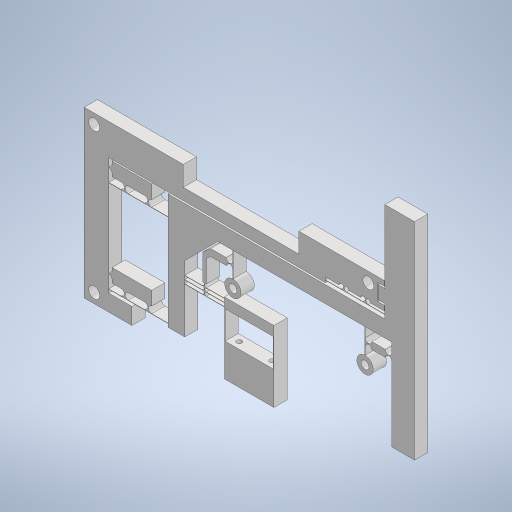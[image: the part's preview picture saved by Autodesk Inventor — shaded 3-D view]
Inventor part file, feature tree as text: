
AUTODESK INVENTOR PART (.ipt)
format: ipt  version: 2023 (Build 270158000, 158)  size: 674,816 bytes
history: native  units: mm
features: reference x11, extrude x9, sketch x8, other x7
ambient origin geometry x8: Origin, YZ Plane, XZ Plane, XY Plane, X Axis, Y Axis, Z Axis, Center Point
bodies: Solid1 (feature_tree)
feature tree (35):
  other  "<userpath>\ClawdDrive\Objet3D\IminaProbe\V3Roue\Settings.xlsx"
  extrude  "Extrusion1"  Depth=20.0mm
  extrude  "Extrusion2"  Depth=4.0mm TaperAngle=0.0deg
  extrude  "Extrusion3"  Depth=0.5mm
  extrude  "Extrusion4"  Depth=5.0mm
  extrude  "Extrusion5"  Depth=18.0mm
  extrude  "Extrusion7"  Depth=1.0mm
  extrude  "Extrusion8"  Depth=1.0mm
  extrude  "Extrusion9"  Depth=0.1mm
  extrude  "Extrusion10"  Depth=5.0mm
  sketch  "Sketch1"  dims[d0=4.0mm d1=0.0mm d2=20.0mm]
  reference  "Reference1"
  sketch  "Sketch2"  dims[d3=9.0mm d4=4.0mm d5=0.0mm]
  sketch  "Sketch6"  dims[d6=7.0mm d7=0.5mm]
  reference  "Reference2"
  sketch  "Sketch7"  dims[d8=4.0mm d9=0.0mm d27=5.0mm]
  sketch  "Sketch9"  dims[d28=30.0mm d29=18.0mm]
  sketch  "Sketch10"  dims[d30=0.1mm d31=1.0mm]
  sketch  "Sketch11"  dims[d32=0.1mm d33=1.0mm]
  reference  "Reference3"
  reference  "Reference4"
  reference  "Reference5"
  reference  "Reference6"
  reference  "Reference7"
  reference  "Reference8"
  sketch  "Sketch12"  dims[d34=15.0mm d35=0.1mm d37=5.0mm d39=5.0mm d40=0.1mm d41=0.1mm d43=0.0mm d44=15.0mm d45=18.0mm d46=2.0mm d47=0.1mm d48=40.0mm d49=2.4mm d50=2.4mm d51=5.0mm d52=5.0mm d53=0.1mm d54=0.05mm d55=0.05mm d56=0.1mm d57=8.0mm d58=0.1mm d59=2.0mm d60=1.5mm d61=5.0mm d62=0.5mm d63=0.5mm d64=0.1mm d65=0.1mm d66=5.0mm d67=0.0mm d68=0.0mm d69=15.0mm d70=10.0mm d71=15.0mm d72=0.0mm d73=1.5mm d74=1.5mm d75=0.2mm d76=0.2mm d79=1.0mm d80=0.1mm d81=0.1mm d82=1.0mm d83=4.0mm d84=0.0mm d87=15.0mm d88=10.0mm d89=10.0mm d90=10.0mm d91=10.0mm d92=0.1mm d93=0.75mm d94=2.0mm d95=1.5mm d97=18.0mm d98=7.0mm d99=4.0mm d100=0.0mm d105=2.0mm d106=6.9mm d107=20.0mm d108=35.0mm d110=6.0mm d111=4.0mm d112=0.0mm d113=2.0mm d114=2.0mm d115=10.0mm d116=2.5mm d117=1.6mm d118=1.6mm d119=10.0mm d120=0.0mm d121=30.0mm d122=10.0mm d123=0.0mm d124=13.0mm d125=3.0mm d126=3.0mm d127=4.0mm d128=3.4mm d129=3.4mm d130=0.1mm d131=7.0mm d132=5.0mm d133=8.0mm d134=0.0mm d135=12.0mm d140=-1.0mm d141=1.0mm d142=2.0mm d143=2.0mm d144=2.1mm d145=2.0mm d146=2.0mm d147=2.1mm d148=0.0mm d149=1.0mm d150=1.0mm d151=2.0mm d152=2.0mm d153=5.0mm d154=1.6mm d155=5.0mm d156=1.6mm d157=1.0mm d158=1.0mm d159=1.0mm d160=1.0mm d161=1.1mm d162=1.1mm d163=5.45mm d164=5.45mm d165=1.0mm d166=1.0mm d167=5.0mm d168=2.0mm d169=2.1mm d170=2.0mm d171=5.0mm d172=2.1mm d173=2.0mm d174=2.0mm d176=2.0mm d177=2.0mm d178=2.1mm d179=2.0mm d180=2.0mm d181=5.0mm d182=2.1mm d183=5.0mm d184=2.1mm d185=2.0mm d186=2.0mm d187=2.0mm d188=2.0mm d189=2.1mm d190=2.1mm d191=2.9mm d192=2.9mm d193=1.1mm d194=0.0mm d24=0.5mm d25=0.872665mm d26=0.5mm]
  reference  "Reference9"
  reference  "Reference10"
  reference  "Reference11"
  other  "<userpath>\ClawdDrive\Objet3D\IminaProbe\V3Roue\RoueV3.iam"
  other  "RoueV3.iam"
  other  "RoueV3partA:1"
  other  "DifferentialLinearActuator:1"
  other  "RoueV3PartC:1"
  other  "DifferentialLinearActuator:5"
